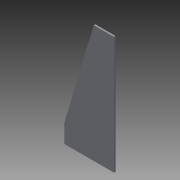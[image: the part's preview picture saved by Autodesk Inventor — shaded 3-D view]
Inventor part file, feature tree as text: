
AUTODESK INVENTOR PART (.ipt)
format: ipt  version: 2013 (Build 170138000, 138)  size: 301,568 bytes
history: native  units: in
note: dims shown in document units (in); Inventor stores cm internally (conversion verified against a paired STEP export)
features: reference x10, extrude x8, sketch x8, plane x1
ambient origin geometry x8: Origin, YZ Plane, XZ Plane, XY Plane, X Axis, Y Axis, Z Axis, Center Point
feature tree (27):
  plane  "Work Plane1"
  extrude  "Extrusion2"  Depth=0.255in TaperAngle=0.0deg
  extrude  "Extrusion5"  Depth=0.9843in
  extrude  "Extrusion6"  Depth=0.1969in TaperAngle=0.0deg
  extrude  "Extrusion7"  Depth=0.5906in
  extrude  "Extrusion8"  Depth=0.1969in TaperAngle=0.0deg
  extrude  "Extrusion9"  Depth=0.0591in
  extrude  "Extrusion10"  Depth=0.0591in
  extrude  "Extrusion4"  Depth=0.0591in
  sketch  "Sketch2"  dims[d3=2.9528in d4=0.255in d5=0.0in]
  reference  "Reference4"
  reference  "Reference5"
  sketch  "Sketch4"  dims[d8=0.5906in d9=0.9843in]
  sketch  "Sketch5"  dims[d10=0.1969in d11=0.0in d12=0.1969in d13=0.0in]
  sketch  "Sketch6"  dims[d14=0.9843in d15=0.5906in]
  sketch  "Sketch7"  dims[d16=0.1969in d17=0.0in d18=0.1969in d19=0.0in]
  reference  "Reference6"
  reference  "Reference7"
  reference  "Reference8"
  reference  "Reference9"
  reference  "Reference10"
  reference  "Reference11"
  reference  "Reference12"
  reference  "Reference13"
  sketch  "Sketch8"  dims[d20=0.0984in d21=0.0591in]
  sketch  "Sketch9"  dims[d22=0.1575in d23=0.0591in d24=0.1575in]
  sketch  "Sketch10"  dims[d25=0.0591in d26=0.1575in d27=0.0591in d28=0.1575in d29=0.0591in d30=0.1575in d31=0.0591in d32=0.1575in d33=0.0984in d34=0.0591in d35=0.1575in d36=0.0591in d37=0.1575in d38=0.0984in d39=0.0984in d40=0.1969in d41=0.0in d42=0.315in d44=4.9213in d45=5.9055in d46=0.1969in d47=0.0in d48=0.1969in d49=0.1969in d50=1.6535in d51=0.8661in d52=1.2205in d53=0.1181in d54=0.7874in d55=0.9843in d56=0.5906in d57=0.1969in d58=0.0in]
